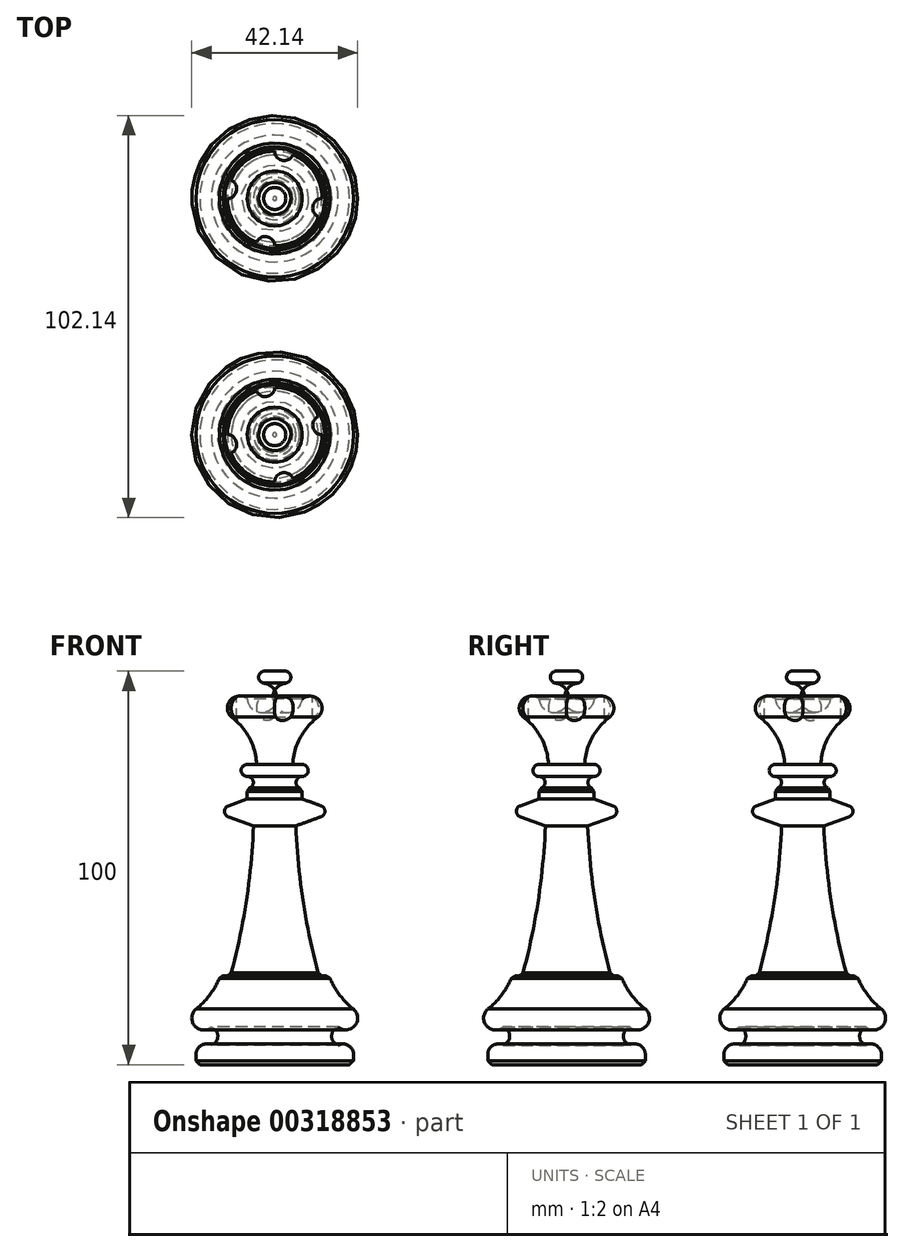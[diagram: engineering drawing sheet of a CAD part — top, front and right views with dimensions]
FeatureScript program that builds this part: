
annotation { "Feature Type Name" : "Feature", "Feature Type Description" : "" }
export const myFeature = defineFeature(function(context is Context, id is Id, definition is map)
    precondition{}
    {
        {
            var Q0;
            Q0=qCreatedBy(makeId("Front.planeOp"),FACE);
            var sketch = newSketch(context, id + "F0", { "sketchPlane" : qUnion([Q0])});
            skLineSegment(sketch, "E0", {"start": v(0, -47) * mm, "end": v(-20, -47) * mm});
            skLineSegment(sketch, "E1", {"start": v(-20, -47) * mm, "end": v(-20, -44.36) * mm});
            skArc(sketch, "E2", {"start": v(-16.1, -42.06) * mm, "mid": v(-18.71, -42.1) * mm, "end": v(-20, -44.36) * mm});
            skArc(sketch, "E3", {"start": v(-16.1, -42.06) * mm, "mid": v(-14.45, -39.76) * mm, "end": v(-16.1, -37.46) * mm});
            skArc(sketch, "E4", {"start": v(-20, -32.86) * mm, "mid": v(-20.36, -37.1) * mm, "end": v(-16.1, -37.46) * mm});
            skArc(sketch, "E5", {"start": v(-20, -32.86) * mm, "mid": v(-16.32, -29.06) * mm, "end": v(-13.8, -24.42) * mm});
            skLineSegment(sketch, "E6", {"start": v(-13.8, -24.42) * mm, "end": v(-11.25, -24.42) * mm});
            skArc(sketch, "E7", {"start": v(-11.25, -24.42) * mm, "mid": v(-7.24, -5.53) * mm, "end": v(-5.37, 13.68) * mm});
            skLineSegment(sketch, "E8", {"start": v(-5.37, 13.68) * mm, "end": v(-11.76, 15.98) * mm});
            skArc(sketch, "E9", {"start": v(-11.76, 18.8) * mm, "mid": v(-12.75, 17.39) * mm, "end": v(-11.76, 15.98) * mm});
            skLineSegment(sketch, "E10", {"start": v(-11.76, 18.8) * mm, "end": v(-6.97, 20.52) * mm});
            skLineSegment(sketch, "E11", {"start": v(-6.97, 20.52) * mm, "end": v(-6.97, 23.18) * mm});
            skArc(sketch, "E12", {"start": v(-6.97, 23.18) * mm, "mid": v(-5.42, 24.7) * mm, "end": v(-6.97, 26.2) * mm});
            skArc(sketch, "E13", {"start": v(-6.97, 29.28) * mm, "mid": v(-8.53, 27.74) * mm, "end": v(-6.97, 26.2) * mm});
            skLineSegment(sketch, "E14", {"start": v(-6.97, 29.28) * mm, "end": v(-4.6, 29.25) * mm});
            skArc(sketch, "E15", {"start": v(-4.6, 29.25) * mm, "mid": v(-6.41, 36) * mm, "end": v(-11, 41.3) * mm});
            skArc(sketch, "E16", {"start": v(-6.97, 45.9) * mm, "mid": v(-11.27, 45.6) * mm, "end": v(-11, 41.3) * mm});
            skArc(sketch, "E17", {"start": v(-2.81, 49.93) * mm, "mid": v(-5.85, 48.9) * mm, "end": v(-6.97, 45.9) * mm});
            skArc(sketch, "E18", {"start": v(-2.81, 53) * mm, "mid": v(-4.1, 51.47) * mm, "end": v(-2.81, 49.93) * mm});
            skLineSegment(sketch, "E19", {"start": v(-2.81, 53) * mm, "end": v(0, 53) * mm});
            skLineSegment(sketch, "E20", {"start": v(0, 70.36) * mm, "end": v(0, 53) * mm, "construction": true});
            skLineSegment(sketch, "E21.trimOffspring", {"start": v(0, -47) * mm, "end": v(0, -60.4) * mm, "construction": true});
            skPoint(sketch, "E22.start.orphan", {"position": v(0, 50) * mm});
            skLineSegment(sketch, "E23", {"start": v(0, 53) * mm, "end": v(0, -47) * mm});
            skLineSegment(sketch, "E24", {"start": v(0, 79.02) * mm, "end": v(0, -79.49) * mm, "construction": true});
            skSolve(sketch);
        }
        {
            var Q0;
            Q0=makeQuery(id+"F0.imprint","IMPRINT",FACE,{"disambiguationData":[TD([[makeQuery(id+"F0.imprint","IMPRINT",EDGE,{"derivedFrom":sQuery(id+"F0.wireOp",EDGE,"E0")}),-1.0]])]});
            var Q1;
            Q1=sQuery(id+"F0.wireOp",EDGE,"E20");
            revolve(context, id + "F1", {"entities" : qUnion([Q0]), "axis" : qUnion([Q1]), "revolveType" : RevolveType.FULL});
        }
        {
            var Q0;
            Q0=makeQuery(id+"F1.opRevolve","SWEPT_EDGE",EDGE,{"disambiguationData":[OSD([sQuery(id+"F0.wireOp",EDGE,"E0"),sQuery(id+"F0.wireOp",EDGE,"E1")])]});
            var Q1;
            Q1=makeQuery(id+"F1.opRevolve","SWEPT_EDGE",EDGE,{"disambiguationData":[OSD([sQuery(id+"F0.wireOp",EDGE,"E4"),sQuery(id+"F0.wireOp",EDGE,"E5")])]});
            var Q2;
            Q2=makeQuery(id+"F1.opRevolve","SWEPT_EDGE",EDGE,{"disambiguationData":[OSD([sQuery(id+"F0.wireOp",EDGE,"E5"),sQuery(id+"F0.wireOp",EDGE,"E6")])]});
            var Q3;
            Q3=makeQuery(id+"F1.opRevolve","SWEPT_EDGE",EDGE,{"disambiguationData":[OSD([sQuery(id+"F0.wireOp",EDGE,"E6"),sQuery(id+"F0.wireOp",EDGE,"E7")])]});
            var Q4;
            Q4=makeQuery(id+"F1.opRevolve","SWEPT_EDGE",EDGE,{"disambiguationData":[OSD([sQuery(id+"F0.wireOp",EDGE,"E11"),sQuery(id+"F0.wireOp",EDGE,"E12")])]});
            chamfer(context, id + "F2", {"entities" : qUnion([Q0, Q1, Q2, Q3, Q4]), "width" : 1 * mm, "tangentPropagation" : true});
        }
        {
            var Q0;
            Q0=makeQuery(id+"F1.opRevolve","SWEPT_FACE",FACE,{"disambiguationData":[OSD([sQuery(id+"F0.wireOp",EDGE,"E19")])]});
            var sketch = newSketch(context, id + "F3", { "sketchPlane" : qUnion([Q0])});
            skCircle(sketch, "E25", {"center": v(0, 0) * mm, "radius": 12.5 * mm});
            skCircle(sketch, "E26.cCircle", {"center": v(0, 0) * mm, "radius": 12.5 * mm, "construction": true});
            skLineSegment(sketch, "E26.0", {"start": v(0, 12.5) * mm, "end": v(4.78, 11.55) * mm});
            skLineSegment(sketch, "E26.1", {"start": v(4.78, 11.55) * mm, "end": v(8.84, 8.84) * mm});
            skLineSegment(sketch, "E26.2", {"start": v(8.84, 8.84) * mm, "end": v(11.55, 4.78) * mm});
            skLineSegment(sketch, "E26.3", {"start": v(11.55, 4.78) * mm, "end": v(12.5, 0) * mm});
            skLineSegment(sketch, "E26.4", {"start": v(12.5, 0) * mm, "end": v(11.55, -4.78) * mm});
            skLineSegment(sketch, "E26.5", {"start": v(11.55, -4.78) * mm, "end": v(8.84, -8.84) * mm});
            skLineSegment(sketch, "E26.6", {"start": v(8.84, -8.84) * mm, "end": v(4.78, -11.55) * mm});
            skLineSegment(sketch, "E26.7", {"start": v(4.78, -11.55) * mm, "end": v(0, -12.5) * mm});
            skLineSegment(sketch, "E26.8", {"start": v(0, -12.5) * mm, "end": v(-4.78, -11.55) * mm});
            skLineSegment(sketch, "E26.9", {"start": v(-4.78, -11.55) * mm, "end": v(-8.84, -8.84) * mm});
            skLineSegment(sketch, "E26.10", {"start": v(-8.84, -8.84) * mm, "end": v(-11.55, -4.78) * mm});
            skLineSegment(sketch, "E26.11", {"start": v(-11.55, -4.78) * mm, "end": v(-12.5, 0) * mm});
            skLineSegment(sketch, "E26.12", {"start": v(-12.5, 0) * mm, "end": v(-11.55, 4.78) * mm});
            skLineSegment(sketch, "E26.13", {"start": v(-11.55, 4.78) * mm, "end": v(-8.84, 8.84) * mm});
            skLineSegment(sketch, "E26.14", {"start": v(-8.84, 8.84) * mm, "end": v(-4.78, 11.55) * mm});
            skLineSegment(sketch, "E26.15", {"start": v(-4.78, 11.55) * mm, "end": v(0, 12.5) * mm});
            skArc(sketch, "E27", {"start": v(0, 12.5) * mm, "mid": v(1.93, 9.71) * mm, "end": v(4.78, 11.55) * mm});
            skArc(sketch, "E28", {"start": v(12.5, 0) * mm, "mid": v(9.71, -1.93) * mm, "end": v(11.55, -4.78) * mm});
            skArc(sketch, "E29", {"start": v(0, -12.5) * mm, "mid": v(-1.93, -9.71) * mm, "end": v(-4.78, -11.55) * mm});
            skArc(sketch, "E30", {"start": v(-12.5, 0) * mm, "mid": v(-9.71, 1.93) * mm, "end": v(-11.55, 4.78) * mm});
            skSolve(sketch);
        }
        {
            var Q0;
            Q0=makeQuery(id+"F3.imprint","IMPRINT",FACE,{"disambiguationData":[TD([[makeQuery(id+"F3.imprint","IMPRINT",EDGE,{"derivedFrom":sQuery(id+"F3.wireOp",EDGE,"E26.12")}),-1.0]])]});
            var Q1;
            Q1=makeQuery(id+"F3.imprint","IMPRINT",FACE,{"disambiguationData":[TD([[makeQuery(id+"F3.imprint","IMPRINT",EDGE,{"derivedFrom":sQuery(id+"F3.wireOp",EDGE,"E26.0")}),-1.0]])]});
            var Q2;
            Q2=makeQuery(id+"F3.imprint","IMPRINT",FACE,{"disambiguationData":[TD([[makeQuery(id+"F3.imprint","IMPRINT",EDGE,{"derivedFrom":sQuery(id+"F3.wireOp",EDGE,"E26.4")}),-1.0]])]});
            var Q3;
            Q3=makeQuery(id+"F3.imprint","IMPRINT",FACE,{"disambiguationData":[TD([[makeQuery(id+"F3.imprint","IMPRINT",EDGE,{"derivedFrom":sQuery(id+"F3.wireOp",EDGE,"E26.8")}),-1.0]])]});
            extrude(context, id + "F4", {"entities" : qUnion([Q0, Q1, Q2, Q3]), "operationType" : NewBodyOperationType.REMOVE, "oppositeDirection" : true, "depth" : 25 * mm});
        }
        {
            var Q0;
            Q0=qCreatedBy(makeId("Front.planeOp"),FACE);
            cPlane(context, id + "F5", {"entities" : qUnion([Q0]), "cplaneType" : CPlaneType.OFFSET, "offset" : 30 * mm, "width" : 150 * mm, "height" : 150 * mm});
        }
        {
            var Q0;
            Q0=makeQuery(id+"F1.opRevolve","SWEPT_BODY",BODY,{"disambiguationData":[OSD([sQuery(id+"F0.wireOp",EDGE,"E0"),sQuery(id+"F0.wireOp",EDGE,"E1"),sQuery(id+"F0.wireOp",EDGE,"E2"),sQuery(id+"F0.wireOp",EDGE,"E3"),sQuery(id+"F0.wireOp",EDGE,"E4"),sQuery(id+"F0.wireOp",EDGE,"E5"),sQuery(id+"F0.wireOp",EDGE,"E6"),sQuery(id+"F0.wireOp",EDGE,"E7"),sQuery(id+"F0.wireOp",EDGE,"E8"),sQuery(id+"F0.wireOp",EDGE,"E9"),sQuery(id+"F0.wireOp",EDGE,"E10"),sQuery(id+"F0.wireOp",EDGE,"E11"),sQuery(id+"F0.wireOp",EDGE,"E12"),sQuery(id+"F0.wireOp",EDGE,"E13"),sQuery(id+"F0.wireOp",EDGE,"E14"),sQuery(id+"F0.wireOp",EDGE,"E15"),sQuery(id+"F0.wireOp",EDGE,"E16"),sQuery(id+"F0.wireOp",EDGE,"E17"),sQuery(id+"F0.wireOp",EDGE,"E18"),sQuery(id+"F0.wireOp",EDGE,"E19"),sQuery(id+"F0.wireOp",EDGE,"E23")])]});
            var Q1;
            Q1=qCreatedBy(id+"F5.planeOp",FACE);
            mirror(context, id + "F6", {"entities" : qUnion([Q0]), "mirrorPlane" : qUnion([Q1])});
        }
    });
